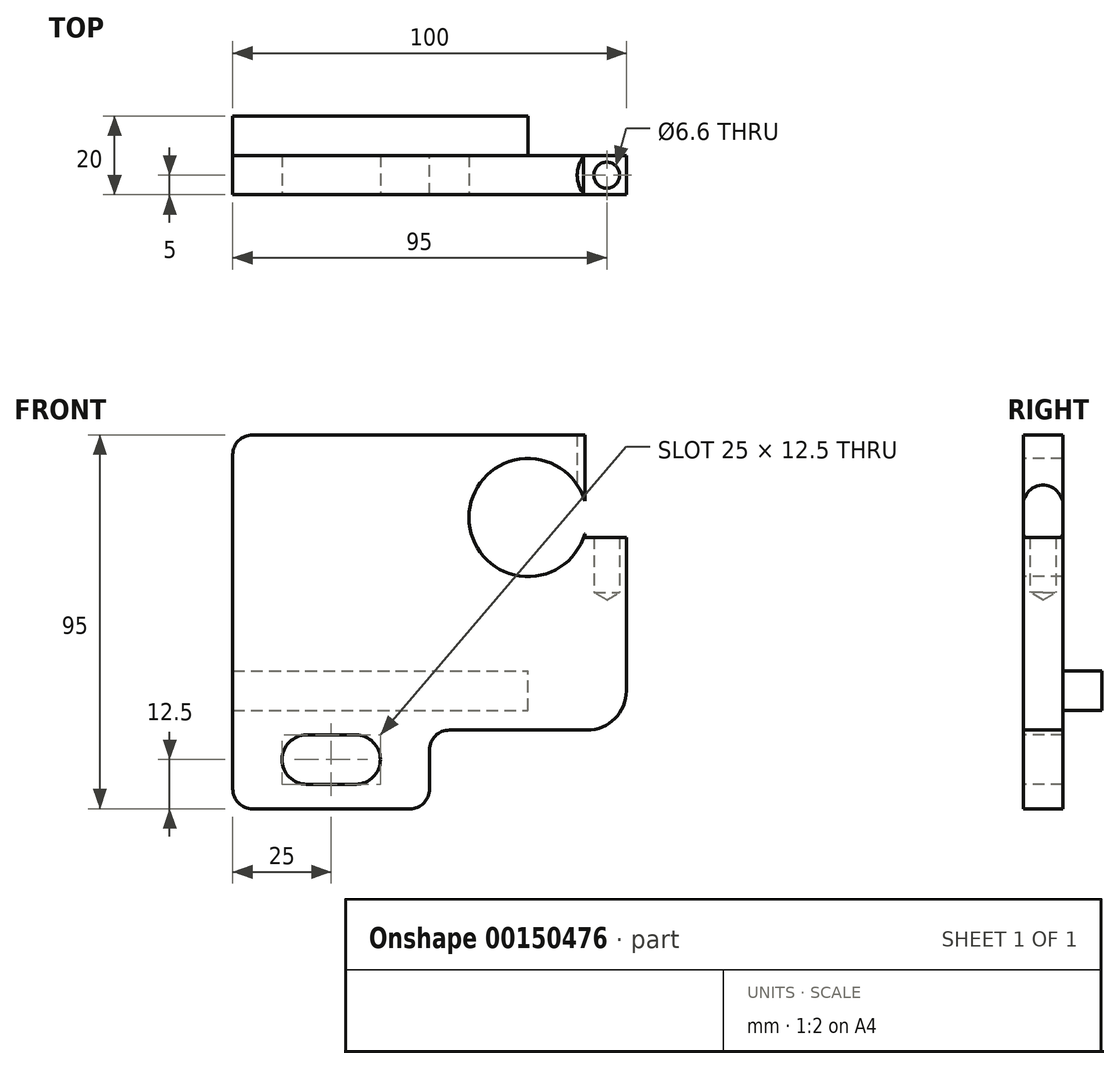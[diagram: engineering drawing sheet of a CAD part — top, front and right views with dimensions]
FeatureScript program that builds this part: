
annotation { "Feature Type Name" : "Feature", "Feature Type Description" : "" }
export const myFeature = defineFeature(function(context is Context, id is Id, definition is map)
    precondition{}
    {
        {
            var Q0;
            Q0=qCreatedBy(makeId("Front.planeOp"),FACE);
            var sketch = newSketch(context, id + "F0", { "sketchPlane" : qUnion([Q0])});
            skLineSegment(sketch, "E0.bottom", {"start": v(0, 0) * mm, "end": v(50, 0) * mm});
            skLineSegment(sketch, "E0.top", {"start": v(0, 95) * mm, "end": v(100, 95) * mm});
            skLineSegment(sketch, "E0.left", {"start": v(0, 0) * mm, "end": v(0, 95) * mm});
            skLineSegment(sketch, "E0.right", {"start": v(100, 20) * mm, "end": v(100, 95) * mm});
            skLineSegment(sketch, "E1", {"start": v(50, 0) * mm, "end": v(50, 20) * mm});
            skLineSegment(sketch, "E2", {"start": v(50, 20) * mm, "end": v(100, 20) * mm});
            skPoint(sketch, "E3.orphan", {"position": v(100, 0) * mm});
            skSolve(sketch);
        }
        {
            var Q0;
            Q0=makeQuery(id+"F0.imprint","IMPRINT",FACE,{"disambiguationData":[TD([[makeQuery(id+"F0.imprint","IMPRINT",EDGE,{"derivedFrom":sQuery(id+"F0.wireOp",EDGE,"E0.bottom")}),1.0]])]});
            extrude(context, id + "F1", {"entities" : qUnion([Q0]), "depth" : 10 * mm});
        }
        {
            var Q0;
            Q0=makeQuery(id+"F1.opExtrude","SWEPT_EDGE",EDGE,{"disambiguationData":[OSD([sQuery(id+"F0.wireOp",EDGE,"E0.right"),sQuery(id+"F0.wireOp",EDGE,"E2")])]});
            fillet(context, id + "F2", {"entities" : qUnion([Q0]), "radius" : 10 * mm, "tangentPropagation" : true, "allowEdgeOverflow" : false});
        }
        {
            var Q0;
            Q0=makeQuery(id+"F1.opExtrude","CAP_FACE",FACE,{"disambiguationData":[OSD([sQuery(id+"F0.wireOp",EDGE,"E0.bottom"),sQuery(id+"F0.wireOp",EDGE,"E0.top"),sQuery(id+"F0.wireOp",EDGE,"E0.left"),sQuery(id+"F0.wireOp",EDGE,"E0.right"),sQuery(id+"F0.wireOp",EDGE,"8Iyojplg-S4F2-Pnly-erZV-muiVhiIIyzsA"),sQuery(id+"F0.wireOp",EDGE,"YJkzzexi-kC4r-bejs-aepH-9CM25obrue70"),sQuery(id+"F0.wireOp",EDGE,"jEWOiXAA-ikGX-Qu3g-tQ5W-ovPbVwimyhUS"),sQuery(id+"F0.wireOp",EDGE,"0f9215f3-c900-42d6-a27c-e8baf503d54a.trimOffspring"),sQuery(id+"F0.wireOp",EDGE,"E1"),sQuery(id+"F0.wireOp",EDGE,"E2")])],"isStart":false});
            var sketch = newSketch(context, id + "F3", { "sketchPlane" : qUnion([Q0])});
            skLineSegment(sketch, "E4.bottom", {"start": v(18.75, 6.25) * mm, "end": v(31.25, 6.25) * mm});
            skLineSegment(sketch, "E4.top", {"start": v(18.75, 18.75) * mm, "end": v(31.25, 18.75) * mm});
            skLineSegment(sketch, "E4.left", {"start": v(12.5, 12.5) * mm, "end": v(12.5, 12.5) * mm});
            skLineSegment(sketch, "E4.right", {"start": v(37.5, 12.5) * mm, "end": v(37.5, 12.5) * mm});
            skPoint(sketch, "E5.visualSharp", {"position": v(12.5, 18.75) * mm});
            skArc(sketch, "E5.filletArc", {"start": v(18.75, 18.75) * mm, "mid": v(14.33, 16.92) * mm, "end": v(12.5, 12.5) * mm});
            skPoint(sketch, "E6.visualSharp", {"position": v(12.5, 6.25) * mm});
            skArc(sketch, "E6.filletArc", {"start": v(12.5, 12.5) * mm, "mid": v(14.33, 8.08) * mm, "end": v(18.75, 6.25) * mm});
            skPoint(sketch, "E7.visualSharp", {"position": v(37.5, 6.25) * mm});
            skArc(sketch, "E7.filletArc", {"start": v(31.25, 6.25) * mm, "mid": v(35.67, 8.08) * mm, "end": v(37.5, 12.5) * mm});
            skPoint(sketch, "E8.visualSharp", {"position": v(37.5, 18.75) * mm});
            skArc(sketch, "E8.filletArc", {"start": v(37.5, 12.5) * mm, "mid": v(35.67, 16.92) * mm, "end": v(31.25, 18.75) * mm});
            skSolve(sketch);
        }
        {
            var Q0;
            Q0=makeQuery(id+"F3.imprint","IMPRINT",FACE,{"disambiguationData":[TD([[makeQuery(id+"F3.imprint","IMPRINT",EDGE,{"derivedFrom":sQuery(id+"F3.wireOp",EDGE,"E4.bottom")}),1.0]])]});
            extrude(context, id + "F4", {"entities" : qUnion([Q0]), "operationType" : NewBodyOperationType.REMOVE, "endBound" : BoundingType.THROUGH_ALL, "oppositeDirection" : true, "depth" : 25 * mm});
        }
        {
            var Q0;
            Q0=makeQuery(id+"F1.opExtrude","SWEPT_EDGE",EDGE,{"disambiguationData":[OSD([sQuery(id+"F0.wireOp",EDGE,"E1"),sQuery(id+"F0.wireOp",EDGE,"E2")])]});
            var Q1;
            Q1=makeQuery(id+"F1.opExtrude","SWEPT_EDGE",EDGE,{"disambiguationData":[OSD([sQuery(id+"F0.wireOp",EDGE,"E0.bottom"),sQuery(id+"F0.wireOp",EDGE,"E1")])]});
            var Q2;
            Q2=makeQuery(id+"F1.opExtrude","SWEPT_EDGE",EDGE,{"disambiguationData":[OSD([sQuery(id+"F0.wireOp",EDGE,"E0.bottom"),sQuery(id+"F0.wireOp",EDGE,"E0.left")])]});
            var Q3;
            Q3=makeQuery(id+"F1.opExtrude","SWEPT_EDGE",EDGE,{"disambiguationData":[OSD([sQuery(id+"F0.wireOp",EDGE,"E0.top"),sQuery(id+"F0.wireOp",EDGE,"E0.left")])]});
            fillet(context, id + "F5", {"entities" : qUnion([Q0, Q1, Q2, Q3]), "radius" : 5 * mm, "tangentPropagation" : true, "allowEdgeOverflow" : false});
        }
        {
            var Q0;
            Q0=makeQuery(id+"F1.opExtrude","CAP_FACE",FACE,{"disambiguationData":[OSD([sQuery(id+"F0.wireOp",EDGE,"E0.bottom"),sQuery(id+"F0.wireOp",EDGE,"E0.top"),sQuery(id+"F0.wireOp",EDGE,"E0.left"),sQuery(id+"F0.wireOp",EDGE,"E0.right"),sQuery(id+"F0.wireOp",EDGE,"8Iyojplg-S4F2-Pnly-erZV-muiVhiIIyzsA"),sQuery(id+"F0.wireOp",EDGE,"YJkzzexi-kC4r-bejs-aepH-9CM25obrue70"),sQuery(id+"F0.wireOp",EDGE,"jEWOiXAA-ikGX-Qu3g-tQ5W-ovPbVwimyhUS"),sQuery(id+"F0.wireOp",EDGE,"0f9215f3-c900-42d6-a27c-e8baf503d54a.trimOffspring"),sQuery(id+"F0.wireOp",EDGE,"E1"),sQuery(id+"F0.wireOp",EDGE,"E2")])],"isStart":true});
            var sketch = newSketch(context, id + "F6", { "sketchPlane" : qUnion([Q0])});
            skLineSegment(sketch, "E9.bottom", {"start": v(0, 25) * mm, "end": v(-75, 25) * mm});
            skLineSegment(sketch, "E9.top", {"start": v(0, 35) * mm, "end": v(-75, 35) * mm});
            skLineSegment(sketch, "E9.left", {"start": v(0, 25) * mm, "end": v(0, 35) * mm});
            skLineSegment(sketch, "E9.right", {"start": v(-75, 25) * mm, "end": v(-75, 35) * mm});
            skSolve(sketch);
        }
        {
            var Q0;
            Q0=makeQuery(id+"F6.imprint","IMPRINT",FACE,{"disambiguationData":[TD([[makeQuery(id+"F6.imprint","IMPRINT",EDGE,{"derivedFrom":sQuery(id+"F6.wireOp",EDGE,"E9.bottom")}),-1.0]])]});
            extrude(context, id + "F7", {"entities" : qUnion([Q0]), "operationType" : NewBodyOperationType.ADD, "depth" : 10 * mm});
        }
        {
            var Q0;
            Q0=makeQuery(id+"F1.opExtrude","CAP_FACE",FACE,{"disambiguationData":[OSD([sQuery(id+"F0.wireOp",EDGE,"E0.bottom"),sQuery(id+"F0.wireOp",EDGE,"E0.top"),sQuery(id+"F0.wireOp",EDGE,"E0.left"),sQuery(id+"F0.wireOp",EDGE,"E0.right"),sQuery(id+"F0.wireOp",EDGE,"E1"),sQuery(id+"F0.wireOp",EDGE,"E2")])],"isStart":false});
            var sketch = newSketch(context, id + "F8", { "sketchPlane" : qUnion([Q0])});
            skArc(sketch, "E10", {"start": v(89.97, 75) * mm, "mid": v(60, 74) * mm, "end": v(89.97, 73) * mm});
            skLineSegment(sketch, "E11", {"start": v(75, 74) * mm, "end": v(100, 74) * mm, "construction": true});
            skLineSegment(sketch, "E12.bottom", {"start": v(89.97, 73) * mm, "end": v(100, 73) * mm});
            skLineSegment(sketch, "E12.top", {"start": v(89.97, 75) * mm, "end": v(100, 75) * mm});
            skLineSegment(sketch, "E12.right", {"start": v(100, 73) * mm, "end": v(100, 75) * mm});
            skPoint(sketch, "E12.left.start.orphan", {"position": v(75, 73) * mm});
            skSolve(sketch);
        }
        {
            var Q0;
            Q0=makeQuery(id+"F8.imprint","IMPRINT",FACE,{"disambiguationData":[TD([[makeQuery(id+"F8.imprint","IMPRINT",EDGE,{"derivedFrom":sQuery(id+"F8.wireOp",EDGE,"E10")}),1.0]])]});
            extrude(context, id + "F9", {"entities" : qUnion([Q0]), "operationType" : NewBodyOperationType.REMOVE, "endBound" : BoundingType.THROUGH_ALL, "oppositeDirection" : true, "depth" : 25 * mm});
        }
        {
            var Q0;
            Q0=makeQuery(id+"F1.opExtrude","SWEPT_FACE",FACE,{"disambiguationData":[OSD([sQuery(id+"F0.wireOp",EDGE,"E0.top")])]});
            var sketch = newSketch(context, id + "F10", { "sketchPlane" : qUnion([Q0])});
            skPoint(sketch, "E13", {"position": v(95, -5) * mm});
            skSolve(sketch);
        }
        {
            var Q0;
            Q0=sQuery(id+"F10.wireOp",VERTEX,"E13");
            var Q1;
            Q1=makeQuery(id+"F1.opExtrude","SWEPT_BODY",BODY,{"disambiguationData":[OSD([sQuery(id+"F0.wireOp",EDGE,"E0.bottom"),sQuery(id+"F0.wireOp",EDGE,"E0.top"),sQuery(id+"F0.wireOp",EDGE,"E0.left"),sQuery(id+"F0.wireOp",EDGE,"E0.right"),sQuery(id+"F0.wireOp",EDGE,"E1"),sQuery(id+"F0.wireOp",EDGE,"E2")])]});
            hole(context, id + "F11", {"style" : HoleStyle.C_BORE, "endStyle" : HoleEndStyle.BLIND, "holeDiameter" : 6.6 * mm, "cBoreDiameter" : 15 * mm, "cBoreDepth" : 6 * mm, "holeDepth" : 20 * mm, "locations" : qUnion([Q0]), "scope" : qUnion([Q1]), "startStyle" : HoleStartStyle.PART});
        }
    });
